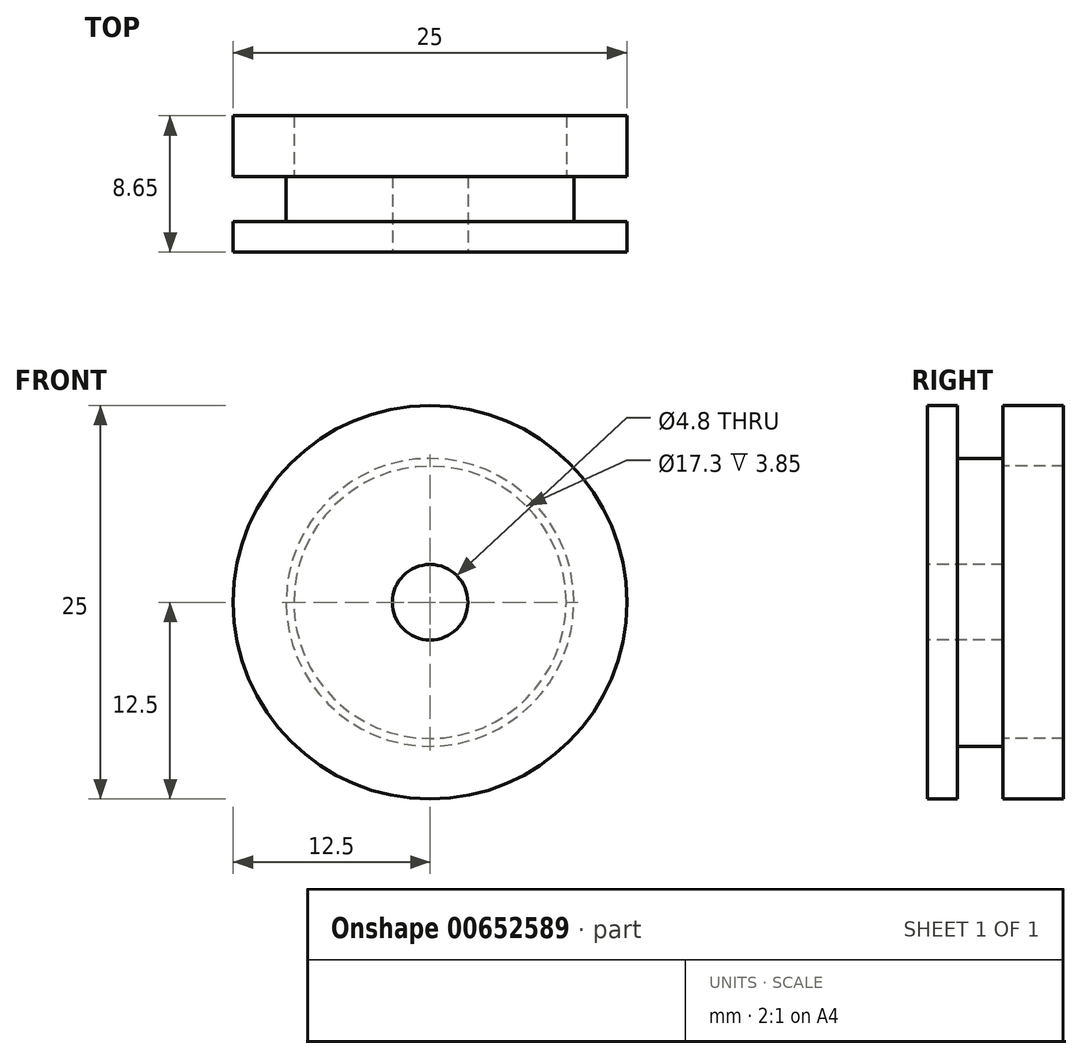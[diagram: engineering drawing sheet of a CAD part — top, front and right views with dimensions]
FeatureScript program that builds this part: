
annotation { "Feature Type Name" : "Feature", "Feature Type Description" : "" }
export const myFeature = defineFeature(function(context is Context, id is Id, definition is map)
    precondition{}
    {
        {
            var Q0;
            Q0=qCreatedBy(makeId("Right.planeOp"),FACE);
            var sketch = newSketch(context, id + "F0", { "sketchPlane" : qUnion([Q0])});
            skLineSegment(sketch, "E0", {"start": v(0, 0) * mm, "end": v(0, 12.5) * mm});
            skLineSegment(sketch, "E1", {"start": v(0, 12.5) * mm, "end": v(1.92, 12.5) * mm});
            skLineSegment(sketch, "E2", {"start": v(1.92, 12.5) * mm, "end": v(1.92, 9.14) * mm});
            skLineSegment(sketch, "E3", {"start": v(1.92, 9.14) * mm, "end": v(4.8, 9.14) * mm});
            skLineSegment(sketch, "E4", {"start": v(4.8, 9.14) * mm, "end": v(4.8, 12.5) * mm});
            skLineSegment(sketch, "E5", {"start": v(4.8, 12.5) * mm, "end": v(8.65, 12.5) * mm});
            skPoint(sketch, "E6.end.orphan", {"position": v(0, 2.4) * mm});
            skLineSegment(sketch, "E7", {"start": v(8.65, 12.5) * mm, "end": v(8.65, 8.65) * mm});
            skLineSegment(sketch, "E8", {"start": v(8.65, 8.65) * mm, "end": v(4.8, 8.65) * mm});
            skLineSegment(sketch, "E9", {"start": v(4.8, 8.65) * mm, "end": v(4.8, 2.4) * mm});
            skLineSegment(sketch, "E10", {"start": v(4.8, 2.4) * mm, "end": v(0, 2.4) * mm});
            skLineSegment(sketch, "E11", {"start": v(0, 0) * mm, "end": v(39.3, 0) * mm, "construction": true});
            skSolve(sketch);
        }
        {
            var Q0;
            Q0 = qSketchRegion(id + "F0", true);
            var Q1;
            Q1=sQuery(id+"F0.wireOp",EDGE,"E11");
            revolve(context, id + "F1", {"entities" : qUnion([Q0]), "axis" : qUnion([Q1]), "revolveType" : RevolveType.FULL});
        }
    });
